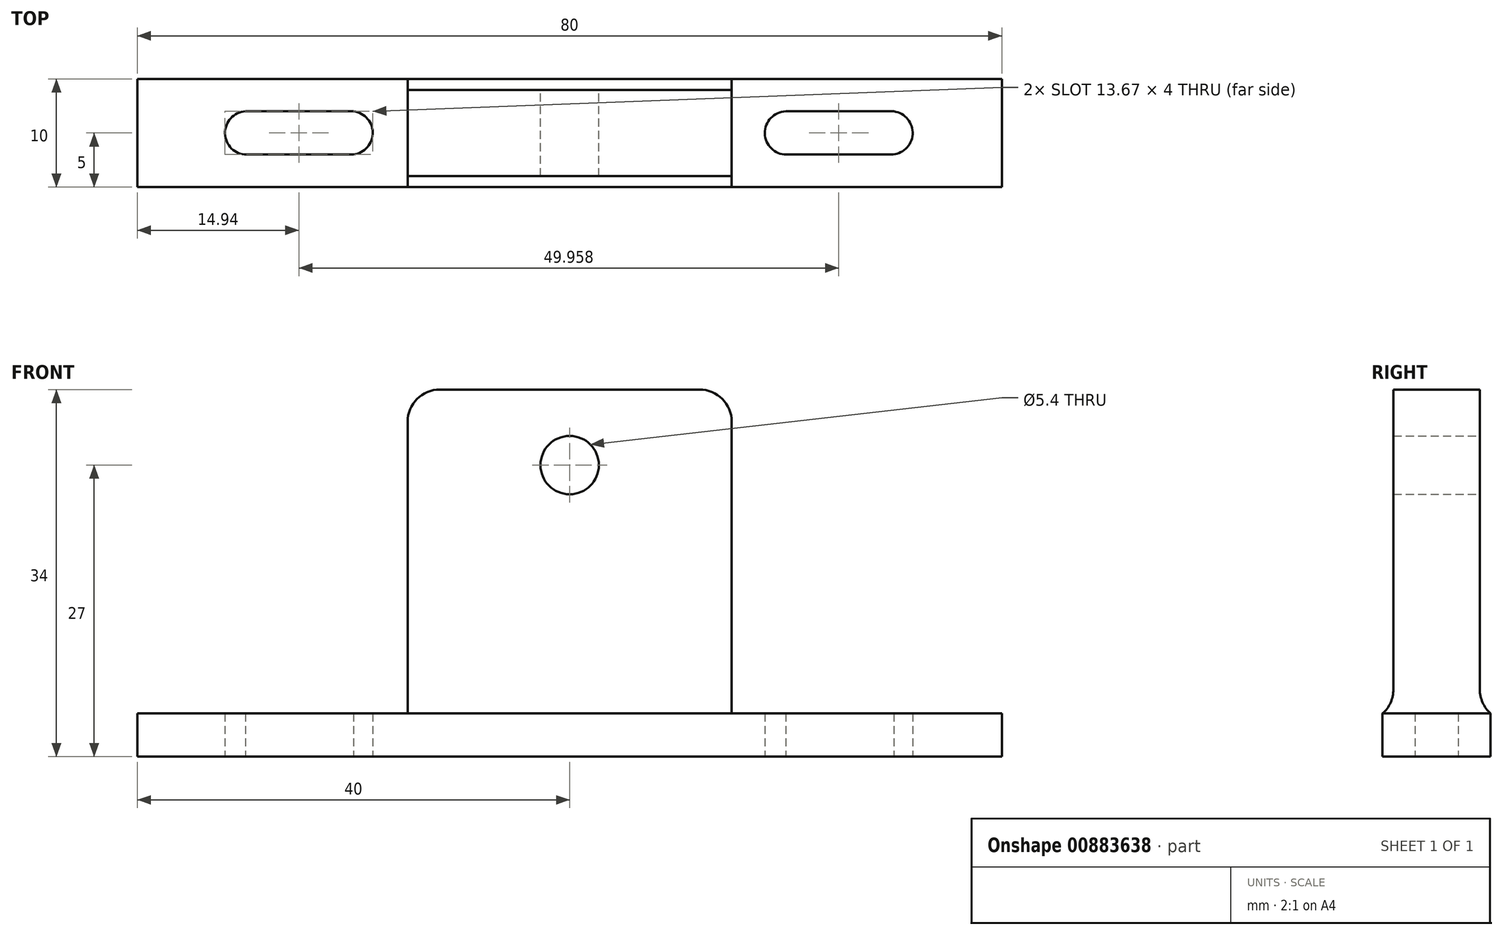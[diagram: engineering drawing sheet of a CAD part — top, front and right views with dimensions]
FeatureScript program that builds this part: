
annotation { "Feature Type Name" : "Feature", "Feature Type Description" : "" }
export const myFeature = defineFeature(function(context is Context, id is Id, definition is map)
    precondition{}
    {
        {
            var Q0;
            Q0=qCreatedBy(makeId("Top.planeOp"),FACE);
            var sketch = newSketch(context, id + "F0", { "sketchPlane" : qUnion([Q0])});
            skPoint(sketch, "E0", {"position": v(-40, 5) * mm});
            skLineSegment(sketch, "E1.bottom", {"start": v(-40, 5) * mm, "end": v(40, 5) * mm});
            skLineSegment(sketch, "E1.top", {"start": v(-40, -5) * mm, "end": v(40, -5) * mm});
            skLineSegment(sketch, "E1.left", {"start": v(-40, 5) * mm, "end": v(-40, -5) * mm});
            skLineSegment(sketch, "E1.right", {"start": v(40, 5) * mm, "end": v(40, -5) * mm});
            skPoint(sketch, "E2", {"position": v(-30, 2) * mm});
            skPoint(sketch, "E3", {"position": v(20, 2) * mm});
            skLineSegment(sketch, "E4.bottom", {"start": v(-30, 2) * mm, "end": v(-20, 2) * mm});
            skLineSegment(sketch, "E4.top", {"start": v(-29.9, -2) * mm, "end": v(-20.23, -2) * mm});
            skLineSegment(sketch, "E5.bottom", {"start": v(20, 2) * mm, "end": v(30, 2) * mm});
            skLineSegment(sketch, "E5.top", {"start": v(20.06, -2) * mm, "end": v(29.73, -2) * mm});
            skArc(sketch, "E6", {"start": v(-29.9, -2) * mm, "mid": v(-31.9, -0.05) * mm, "end": v(-30, 2) * mm});
            skArc(sketch, "E7", {"start": v(-20.23, -2) * mm, "mid": v(-18.22, -0.1) * mm, "end": v(-20, 2) * mm});
            skArc(sketch, "E8", {"start": v(20.06, -2) * mm, "mid": v(18.06, -0.03) * mm, "end": v(20, 2) * mm});
            skArc(sketch, "E9", {"start": v(29.73, -2) * mm, "mid": v(31.74, -0.13) * mm, "end": v(30, 2) * mm});
            skPoint(sketch, "E10", {"position": v(25, 0) * mm});
            skPoint(sketch, "E11", {"position": v(-25, 0) * mm});
            skSolve(sketch);
        }
        {
            var Q0;
            Q0=qCreatedBy(makeId("Front.planeOp"),FACE);
            var sketch = newSketch(context, id + "F1", { "sketchPlane" : qUnion([Q0])});
            skPoint(sketch, "E12", {"position": v(-15, 34) * mm});
            skLineSegment(sketch, "E13.bottom", {"start": v(-15, 34) * mm, "end": v(15, 34) * mm});
            skLineSegment(sketch, "E13.top", {"start": v(-15, 0) * mm, "end": v(15, 0) * mm});
            skLineSegment(sketch, "E13.left", {"start": v(-15, 34) * mm, "end": v(-15, 0) * mm});
            skLineSegment(sketch, "E13.right", {"start": v(15, 34) * mm, "end": v(15, 0) * mm});
            skPoint(sketch, "E14", {"position": v(0, 27) * mm});
            skCircle(sketch, "E15", {"center": v(0, 27) * mm, "radius": 2.7 * mm});
            skSolve(sketch);
        }
        {
            var Q0;
            Q0=makeQuery(id+"F0.imprint","IMPRINT",FACE,{"disambiguationData":[TD([[makeQuery(id+"F0.imprint","IMPRINT",EDGE,{"derivedFrom":sQuery(id+"F0.wireOp",EDGE,"E1.bottom")}),-1.0]])]});
            extrude(context, id + "F2", {"entities" : qUnion([Q0]), "depth" : 4 * mm, "offsetDistance" : 25 * mm});
        }
        {
            var Q0;
            Q0=makeQuery(id+"F1.imprint","IMPRINT",FACE,{"disambiguationData":[TD([[makeQuery(id+"F1.imprint","IMPRINT",EDGE,{"derivedFrom":sQuery(id+"F1.wireOp",EDGE,"E13.bottom")}),-1.0]])]});
            extrude(context, id + "F3", {"entities" : qUnion([Q0]), "operationType" : NewBodyOperationType.ADD, "endBound" : BoundingType.SYMMETRIC, "depth" : 8 * mm, "offsetDistance" : 25 * mm});
        }
        {
            var Q0;
            Q0=makeQuery(id+"F3.boolean.opBoolean","INTERSECT",EDGE,{"derivedFrom":[makeQuery(id+"F2.opExtrude","CAP_FACE",FACE,{"disambiguationData":[OSD([sQuery(id+"F0.wireOp",EDGE,"E1.bottom"),sQuery(id+"F0.wireOp",EDGE,"E1.top"),sQuery(id+"F0.wireOp",EDGE,"E1.left"),sQuery(id+"F0.wireOp",EDGE,"E1.right"),sQuery(id+"F0.wireOp",EDGE,"E4.bottom"),sQuery(id+"F0.wireOp",EDGE,"E4.top"),sQuery(id+"F0.wireOp",EDGE,"E5.bottom"),sQuery(id+"F0.wireOp",EDGE,"E5.top"),sQuery(id+"F0.wireOp",EDGE,"E6"),sQuery(id+"F0.wireOp",EDGE,"E7"),sQuery(id+"F0.wireOp",EDGE,"E8"),sQuery(id+"F0.wireOp",EDGE,"E9")])],"isStart":false}),makeQuery(id+"F3.opExtrude","CAP_FACE",FACE,{"disambiguationData":[OSD([sQuery(id+"F1.wireOp",EDGE,"E13.bottom"),sQuery(id+"F1.wireOp",EDGE,"E13.top"),sQuery(id+"F1.wireOp",EDGE,"E13.left"),sQuery(id+"F1.wireOp",EDGE,"E13.right"),sQuery(id+"F1.wireOp",EDGE,"E15")])],"isStart":false})]});
            var Q1;
            Q1=makeQuery(id+"F3.boolean.opBoolean","INTERSECT",EDGE,{"derivedFrom":[makeQuery(id+"F2.opExtrude","CAP_FACE",FACE,{"disambiguationData":[OSD([sQuery(id+"F0.wireOp",EDGE,"E1.bottom"),sQuery(id+"F0.wireOp",EDGE,"E1.top"),sQuery(id+"F0.wireOp",EDGE,"E1.left"),sQuery(id+"F0.wireOp",EDGE,"E1.right"),sQuery(id+"F0.wireOp",EDGE,"E4.bottom"),sQuery(id+"F0.wireOp",EDGE,"E4.top"),sQuery(id+"F0.wireOp",EDGE,"E5.bottom"),sQuery(id+"F0.wireOp",EDGE,"E5.top"),sQuery(id+"F0.wireOp",EDGE,"E6"),sQuery(id+"F0.wireOp",EDGE,"E7"),sQuery(id+"F0.wireOp",EDGE,"E8"),sQuery(id+"F0.wireOp",EDGE,"E9")])],"isStart":false}),makeQuery(id+"F3.opExtrude","CAP_FACE",FACE,{"disambiguationData":[OSD([sQuery(id+"F1.wireOp",EDGE,"E13.bottom"),sQuery(id+"F1.wireOp",EDGE,"E13.top"),sQuery(id+"F1.wireOp",EDGE,"E13.left"),sQuery(id+"F1.wireOp",EDGE,"E13.right"),sQuery(id+"F1.wireOp",EDGE,"E15")])],"isStart":true})]});
            var Q2;
            Q2=makeQuery(id+"F3.opExtrude","SWEPT_EDGE",EDGE,{"disambiguationData":[OSD([sQuery(id+"F1.wireOp",EDGE,"E13.bottom"),sQuery(id+"F1.wireOp",EDGE,"E13.right")])]});
            var Q3;
            Q3=makeQuery(id+"F3.opExtrude","SWEPT_EDGE",EDGE,{"disambiguationData":[OSD([sQuery(id+"F1.wireOp",EDGE,"E13.bottom"),sQuery(id+"F1.wireOp",EDGE,"E13.left")])]});
            fillet(context, id + "F4", {"entities" : qUnion([Q0, Q1, Q2, Q3]), "radius" : 3 * mm, "tangentPropagation" : true, "allowEdgeOverflow" : false});
        }
    });
